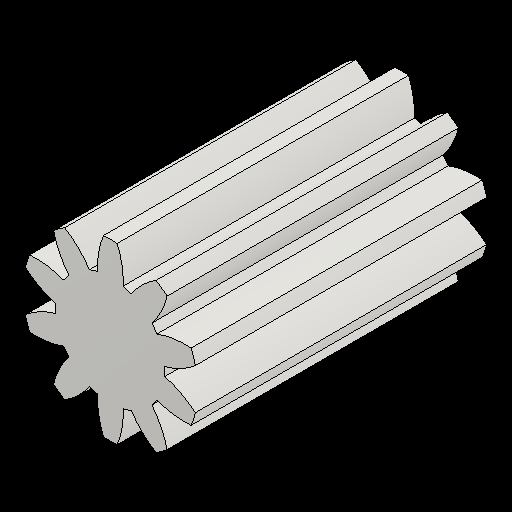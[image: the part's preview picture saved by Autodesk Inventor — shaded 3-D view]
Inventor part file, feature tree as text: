
AUTODESK INVENTOR PART (.ipt)
format: ipt  version: 2023.2 (Build 272271030, 271C)  size: 188,416 bytes
history: native  units: mm (DEFAULTED — no unit token found)
features: plane x3, other x3, sketch x2, extrude x1
ambient origin geometry x8: Origin, YZ Plane, XZ Plane, XY Plane, X Axis, Y Axis, Z Axis, Center Point
bodies: Solid1 (feature_tree)
feature tree (9):
  extrude  "Extrusion1"  Depth=20.0mm TaperAngle=0.0deg
  plane  "Work Plane2"
  plane  "Work Plane8"
  plane  "Work Plane9"
  other  "Spur Gear"
  sketch  "Sketch1"  dims[d0=12.0mm d1=20.0mm d2=0.0mm]
  sketch  "Sketch2"  dims[d3=10.0mm d4=10.0mm d5=0.0mm d16=7.5mm d17=0.0mm d34=3.141593mm d39=0.0mm d41=0.0mm d43=7.5mm d46=7.5mm d47=0.0mm d48=0.0mm]
  other  "Srf1"
  other  "Pitch Diameter"
